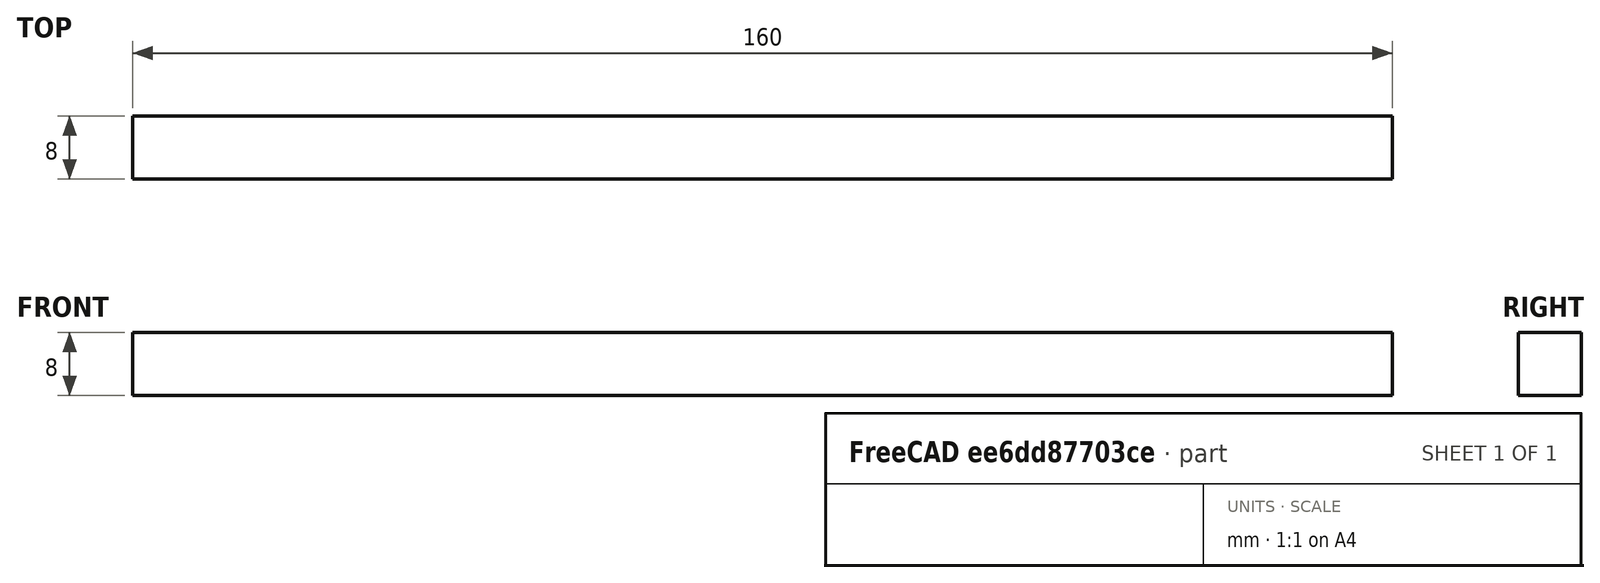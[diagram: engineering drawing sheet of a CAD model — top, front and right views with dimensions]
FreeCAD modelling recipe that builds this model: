
FCSTD DOCUMENT  (FreeCAD 0.19R)
Label: dry box pin
License: All rights reserved
LicenseURL: http://en.wikipedia.org/wiki/All_rights_reserved
objects: Sketcher::SketchObject×1, PartDesign::Pad×1, PartDesign::Body×1
note: 4 computed .brp shape members not serialized (recipe doc carries the construction recipe); baked Part::Feature solids carry a one-line shape summary decoded from their .brp

FEATURE [Sketcher::SketchObject] Sketch
  FullyConstrained = true
  MapMode = 5
  Placement = pos=(0,0,0) rot=(0.57735,0.57735,0.57735;2.0944rad)
  Support = -> [YZ_Plane]
  sketch-geometry (4):
    g0: LineSegment StartX=-4 StartY=4 StartZ=0 EndX=4 EndY=4 EndZ=0
    g1: LineSegment StartX=4 StartY=4 StartZ=0 EndX=4 EndY=-4 EndZ=0
    g2: LineSegment StartX=4 StartY=-4 StartZ=0 EndX=-4 EndY=-4 EndZ=0
    g3: LineSegment StartX=-4 StartY=-4 StartZ=0 EndX=-4 EndY=4 EndZ=0
  constraints (11):
    c: Coincident(g0,g1)
    c: Coincident(g1,g2)
    c: Coincident(g2,g3)
    c: Coincident(g3,g0)
    c: Horizontal(g0)
    c: Horizontal(g2)
    c: Vertical(g1)
    c: Vertical(g3)
    c: Equal(g1,g0)
    c: Symmetric(g0,g1,g-1)
    c: DistanceX(g0,g0) = 8
FEATURE [PartDesign::Pad] Pad
  Direction = (1,1,1)
  Length = 160
  Length2 = 100
  Placement = pos=(0,0,0) rot=(0.57735,0.57735,0.57735;2.0944rad)
  Profile = -> Sketch
  Type = 0
FEATURE [PartDesign::Body] Body
  Group = -> [Sketch,Pad]
  Origin = -> Origin
  Tip = -> Pad
